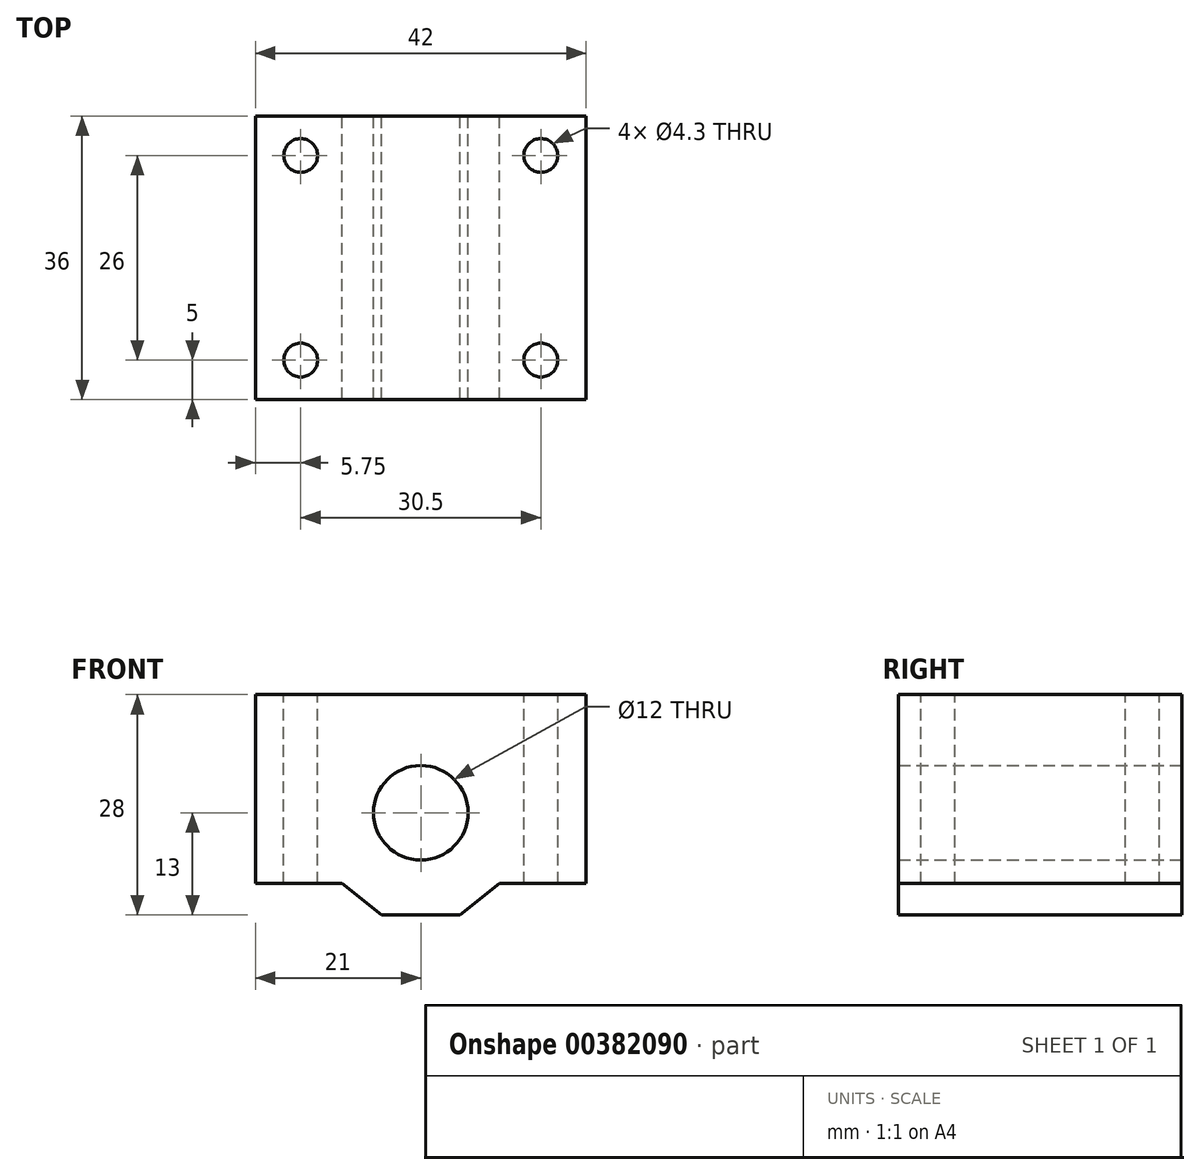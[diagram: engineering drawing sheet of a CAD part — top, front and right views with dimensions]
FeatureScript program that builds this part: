
annotation { "Feature Type Name" : "Feature", "Feature Type Description" : "" }
export const myFeature = defineFeature(function(context is Context, id is Id, definition is map)
    precondition{}
    {
        {
            var Q0;
            Q0=qCreatedBy(makeId("Front.planeOp"),FACE);
            var sketch = newSketch(context, id + "F0", { "sketchPlane" : qUnion([Q0])});
            skCircle(sketch, "E0", {"center": v(0, 0) * mm, "radius": 6 * mm});
            skLineSegment(sketch, "E1.bottom", {"start": v(-21, 15) * mm, "end": v(21, 15) * mm});
            skLineSegment(sketch, "E1.top", {"start": v(-21, -9) * mm, "end": v(-10, -9) * mm});
            skLineSegment(sketch, "E1.left", {"start": v(-21, 15) * mm, "end": v(-21, -9) * mm});
            skLineSegment(sketch, "E1.right", {"start": v(21, 15) * mm, "end": v(21, -9) * mm});
            skLineSegment(sketch, "E2", {"start": v(-10, -9) * mm, "end": v(-5, -13) * mm});
            skLineSegment(sketch, "E3", {"start": v(-5, -13) * mm, "end": v(0, -13) * mm});
            skLineSegment(sketch, "E4.MirrorCS", {"start": v(5, -13) * mm, "end": v(0, -13) * mm});
            skLineSegment(sketch, "E5.MirrorCS", {"start": v(10, -9) * mm, "end": v(5, -13) * mm});
            skLineSegment(sketch, "E6.trimOffspring", {"start": v(10, -9) * mm, "end": v(21, -9) * mm});
            skSolve(sketch);
        }
        {
            var Q0;
            Q0=makeQuery(id+"F0.imprint","IMPRINT",FACE,{"disambiguationData":[TD([[makeQuery(id+"F0.imprint","IMPRINT",EDGE,{"derivedFrom":sQuery(id+"F0.wireOp",EDGE,"E0")}),-1.0]])]});
            extrude(context, id + "F1", {"entities" : qUnion([Q0]), "endBound" : BoundingType.SYMMETRIC, "depth" : 36 * mm, "hasSecondDirection" : true, "secondDirectionOppositeDirection" : true, "secondDirectionDepth" : 18 * mm});
        }
        {
            var Q0;
            Q0=makeQuery(id+"F1.opExtrude","SWEPT_FACE",FACE,{"disambiguationData":[OSD([sQuery(id+"F0.wireOp",EDGE,"E1.bottom")])]});
            var sketch = newSketch(context, id + "F2", { "sketchPlane" : qUnion([Q0])});
            skPoint(sketch, "E7", {"position": v(-15.25, 13) * mm});
            skPoint(sketch, "E8.MirrorP", {"position": v(15.25, 13) * mm});
            skPoint(sketch, "E9.MirrorP", {"position": v(-15.25, -13) * mm});
            skPoint(sketch, "E10.MirrorP", {"position": v(15.25, -13) * mm});
            skSolve(sketch);
        }
        {
            var Q0;
            Q0=sQuery(id+"F2.wireOp",VERTEX,"E7");
            var Q1;
            Q1=sQuery(id+"F2.wireOp",VERTEX,"E8.MirrorP");
            var Q2;
            Q2=sQuery(id+"F2.wireOp",VERTEX,"E10.MirrorP");
            var Q3;
            Q3=sQuery(id+"F2.wireOp",VERTEX,"E9.MirrorP");
            var Q4;
            Q4=makeQuery(id+"F1.opExtrude","SWEPT_BODY",BODY,{"disambiguationData":[OSD([sQuery(id+"F0.wireOp",EDGE,"E0"),sQuery(id+"F0.wireOp",EDGE,"E1.bottom"),sQuery(id+"F0.wireOp",EDGE,"E1.top"),sQuery(id+"F0.wireOp",EDGE,"E1.left"),sQuery(id+"F0.wireOp",EDGE,"E1.right"),sQuery(id+"F0.wireOp",EDGE,"E2"),sQuery(id+"F0.wireOp",EDGE,"E3"),sQuery(id+"F0.wireOp",EDGE,"E4.MirrorCS"),sQuery(id+"F0.wireOp",EDGE,"E5.MirrorCS"),sQuery(id+"F0.wireOp",EDGE,"E6.trimOffspring")])]});
            hole(context, id + "F3", {"style" : HoleStyle.SIMPLE, "endStyle" : HoleEndStyle.THROUGH, "holeDiameter" : 4.3 * mm, "isTappedThrough" : true, "tappedDepth" : 3 * mm, "tapClearance" : 3, "locations" : qUnion([Q0, Q1, Q2, Q3]), "scope" : qUnion([Q4])});
        }
    });
